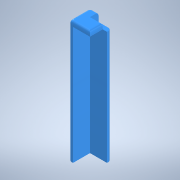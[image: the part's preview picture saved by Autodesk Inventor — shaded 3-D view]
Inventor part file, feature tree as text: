
AUTODESK INVENTOR PART (.ipt)
format: ipt  version: 2021 (Build 250183000, 183)  size: 160,768 bytes
history: native  units: mm
features: extrude x5, sketch x4, fillet x1
ambient origin geometry x8: Origin, YZ Plane, XZ Plane, XY Plane, X Axis, Y Axis, Z Axis, Center Point
bodies: Solid1 (feature_tree)
feature tree (10):
  extrude  "Extrusion1"  Depth=15.0mm
  extrude  "Extrusion3"  Depth=3.0mm
  extrude  "Extrusion4"  Depth=12.0mm
  fillet  "Fillet3"  Radius=3.0mm
  extrude  "Extrusion7"  Depth=12.0mm TaperAngle=0.0deg
  extrude  "Extrusion8"  Depth=2.0mm
  sketch  "Sketch4"  dims[d0=15.0mm d1=15.0mm]
  sketch  "Sketch6"  dims[d2=86.0mm d3=0.0mm d10=3.0mm]
  sketch  "Sketch11"  dims[d11=12.0mm d12=12.0mm d13=3.0mm]
  sketch  "Sketch12"  dims[d14=3.0mm d15=0.0mm d16=12.0mm d17=0.0mm d18=2.0mm d31=6.0mm d32=0.0mm d39=0.0mm d40=0.0mm]
